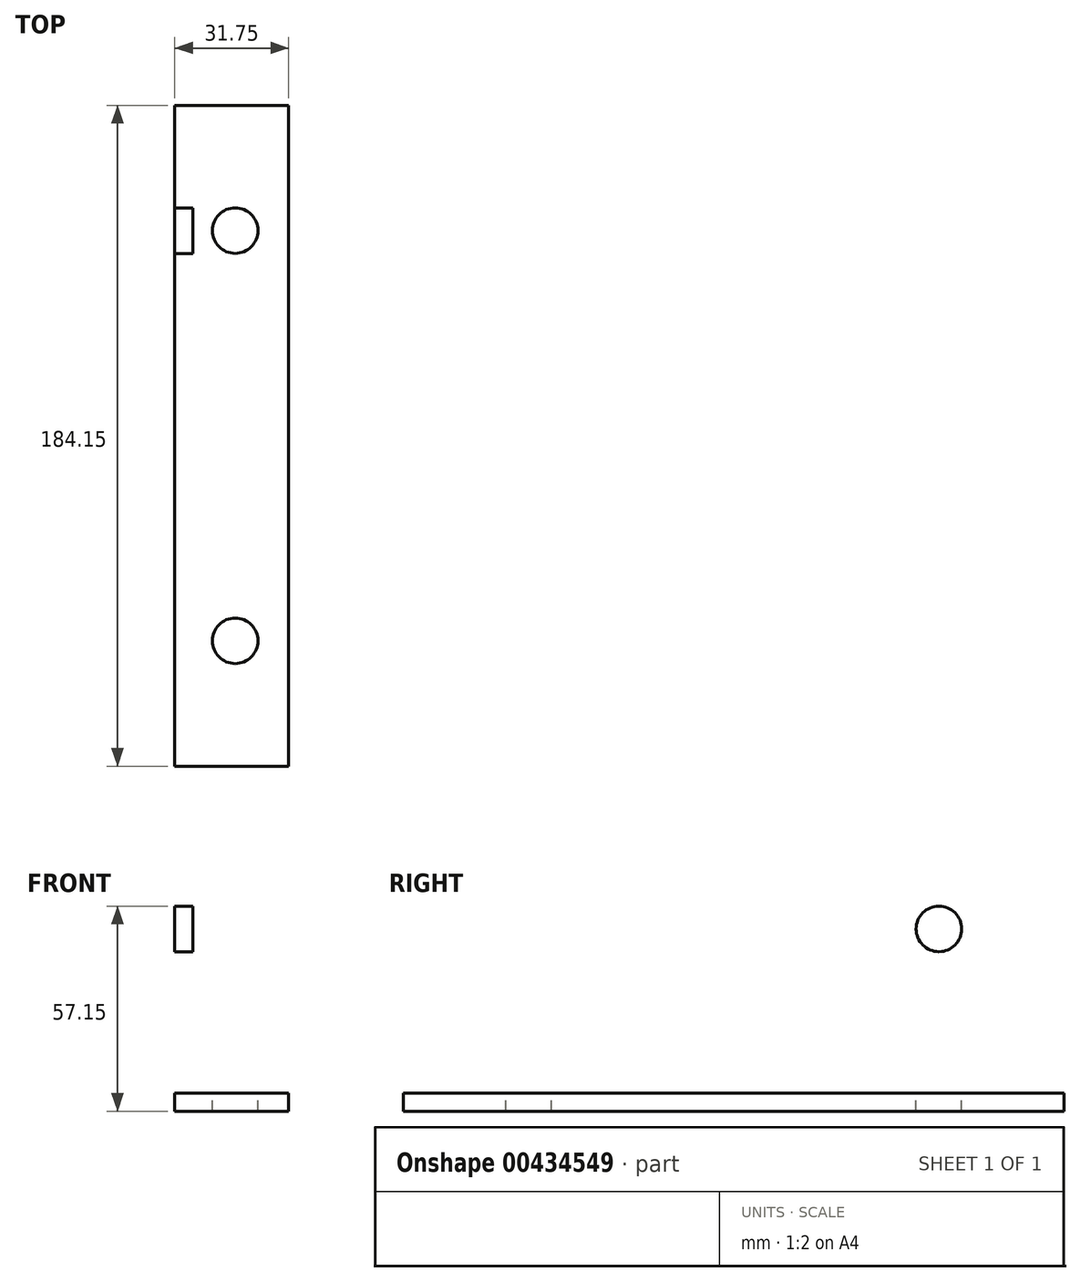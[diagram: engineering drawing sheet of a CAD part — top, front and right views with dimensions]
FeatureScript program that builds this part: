
annotation { "Feature Type Name" : "Feature", "Feature Type Description" : "" }
export const myFeature = defineFeature(function(context is Context, id is Id, definition is map)
    precondition{}
    {
        {
            var Q0;
            Q0=qCreatedBy(makeId("Front.planeOp"),FACE);
            var sketch = newSketch(context, id + "F0", { "sketchPlane" : qUnion([Q0])});
            skLineSegment(sketch, "E0.bottom", {"start": v(0, 0) * mm, "end": v(-5.08, 0) * mm});
            skLineSegment(sketch, "E0.top", {"start": v(0, 55.25) * mm, "end": v(-5.08, 55.25) * mm});
            skLineSegment(sketch, "E0.left", {"start": v(0, 0) * mm, "end": v(0, 55.24) * mm});
            skLineSegment(sketch, "E0.right", {"start": v(-5.08, 0) * mm, "end": v(-5.08, 55.25) * mm});
            skLineSegment(sketch, "E1.bottom", {"start": v(0, 0) * mm, "end": v(26.67, 0) * mm});
            skLineSegment(sketch, "E1.top", {"start": v(-5.08, -5.08) * mm, "end": v(26.67, -5.08) * mm});
            skLineSegment(sketch, "E1.left", {"start": v(-5.08, 0) * mm, "end": v(-5.08, -5.08) * mm});
            skLineSegment(sketch, "E1.right", {"start": v(26.67, 0) * mm, "end": v(26.67, -5.08) * mm});
            skSolve(sketch);
        }
        {
            var Q0;
            Q0 = qSketchRegion(id + "F0", true);
            extrude(context, id + "F1", {"entities" : qUnion([Q0]), "depth" : 184.15 * mm});
        }
        {
            var Q0;
            Q0=makeQuery(id+"F1.opExtrude","SWEPT_FACE",FACE,{"disambiguationData":[OSD([sQuery(id+"F0.wireOp",EDGE,"E0.left")])]});
            var sketch = newSketch(context, id + "F2", { "sketchPlane" : qUnion([Q0])});
            skCircle(sketch, "E2", {"center": v(-149.22, 45.72) * mm, "radius": 6.35 * mm});
            skPoint(sketch, "E3", {"position": v(-92.08, 9.11) * mm});
            skPoint(sketch, "E4", {"position": v(-212.73, 9.11) * mm});
            skCircle(sketch, "E5.MirrorC", {"center": v(-34.93, 45.72) * mm, "radius": 6.35 * mm});
            skSolve(sketch);
        }
        {
            var Q0;
            Q0=makeQuery(id+"F2.imprint","IMPRINT",FACE,{"disambiguationData":[TD([[makeQuery(id+"F2.imprint","IMPRINT",EDGE,{"derivedFrom":sQuery(id+"F2.wireOp",EDGE,"E2")}),1.0]])]});
            var Q1;
            Q1=makeQuery(id+"F2.imprint","IMPRINT",FACE,{"disambiguationData":[TD([[makeQuery(id+"F2.imprint","IMPRINT",EDGE,{"derivedFrom":sQuery(id+"F2.wireOp",EDGE,"E5.MirrorC")}),-1.0]])]});
            extrude(context, id + "F3", {"entities" : qUnion([Q0, Q1]), "operationType" : NewBodyOperationType.REMOVE, "oppositeDirection" : true, "depth" : 25.4 * mm});
        }
        {
            var Q0;
            Q0=makeQuery(id+"F1.opExtrude","SWEPT_FACE",FACE,{"disambiguationData":[OSD([sQuery(id+"F0.wireOp",EDGE,"E1.bottom")])]});
            var sketch = newSketch(context, id + "F4", { "sketchPlane" : qUnion([Q0])});
            skCircle(sketch, "E6", {"center": v(11.75, -149.22) * mm, "radius": 6.35 * mm});
            skLineSegment(sketch, "E7", {"start": v(26.67, -92.08) * mm, "end": v(0, -92.08) * mm});
            skPoint(sketch, "E8", {"position": v(11.75, -212.72) * mm});
            skCircle(sketch, "E9.MirrorC", {"center": v(11.75, -34.93) * mm, "radius": 6.35 * mm});
            skSolve(sketch);
        }
        {
            var Q0;
            Q0 = qSketchRegion(id + "F4", true);
            extrude(context, id + "F5", {"entities" : qUnion([Q0]), "operationType" : NewBodyOperationType.REMOVE, "oppositeDirection" : true, "depth" : 25.4 * mm});
        }
    });
